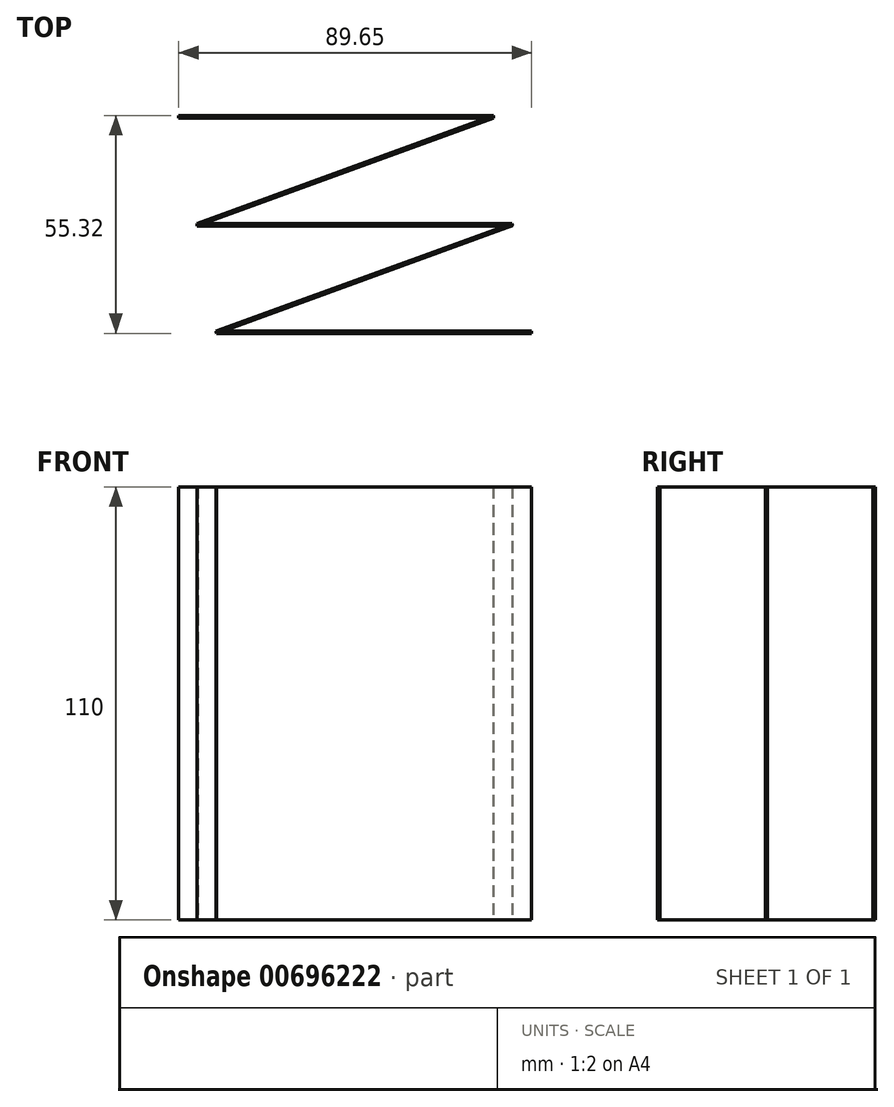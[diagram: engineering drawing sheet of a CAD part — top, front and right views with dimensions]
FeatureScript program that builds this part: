
annotation { "Feature Type Name" : "Feature", "Feature Type Description" : "" }
export const myFeature = defineFeature(function(context is Context, id is Id, definition is map)
    precondition{}
    {
        {
            var Q0;
            Q0=qCreatedBy(makeId("Front.planeOp"),FACE);
            var sketch = newSketch(context, id + "F0", { "sketchPlane" : qUnion([Q0])});
            skLineSegment(sketch, "E0.bottom", {"start": v(40, 55) * mm, "end": v(-40, 55) * mm});
            skLineSegment(sketch, "E0.top", {"start": v(40, -55) * mm, "end": v(-40, -55) * mm});
            skLineSegment(sketch, "E0.left", {"start": v(40, 55) * mm, "end": v(40, -55) * mm});
            skLineSegment(sketch, "E0.right", {"start": v(-40, 55) * mm, "end": v(-40, -55) * mm});
            skPoint(sketch, "E0.middle", {"position": v(0, 0) * mm});
            skSolve(sketch);
        }
        {
            var Q0;
            Q0=makeQuery(id+"F0.imprint","IMPRINT",FACE,{"disambiguationData":[TD([[makeQuery(id+"F0.imprint","IMPRINT",EDGE,{"derivedFrom":sQuery(id+"F0.wireOp",EDGE,"E0.bottom")}),1.0]])]});
            extrude(context, id + "F1", {"entities" : qUnion([Q0]), "depth" : 0.6 * mm, "offsetDistance" : 25 * mm});
        }
        {
            var Q0;
            Q0=makeQuery(id+"F1.opExtrude","SWEPT_BODY",BODY,{"disambiguationData":[OSD([sQuery(id+"F0.wireOp",EDGE,"E0.bottom"),sQuery(id+"F0.wireOp",EDGE,"E0.top"),sQuery(id+"F0.wireOp",EDGE,"E0.left"),sQuery(id+"F0.wireOp",EDGE,"E0.right")])]});
            var Q1;
            Q1=makeQuery(id+"F1.opExtrude","CAP_EDGE",EDGE,{"disambiguationData":[OSD([sQuery(id+"F0.wireOp",EDGE,"E0.right")])],"isStart":false});
            circularPattern(context, id + "F2", {"entities" : qUnion([Q0]), "axis" : qUnion([Q1]), "angle" : 20 * degree, "instanceCount" : 2, "oppositeDirection" : true, "equalSpace" : true});
        }
        {
            var Q0;
            Q0=makeQuery(id+"F2.opPattern","COPY",BODY,{"derivedFrom":makeQuery(id+"F1.opExtrude","SWEPT_BODY",BODY,{"disambiguationData":[OSD([sQuery(id+"F0.wireOp",EDGE,"E0.bottom"),sQuery(id+"F0.wireOp",EDGE,"E0.top"),sQuery(id+"F0.wireOp",EDGE,"E0.left"),sQuery(id+"F0.wireOp",EDGE,"E0.right")])]}),"instanceName":"1"});
            var Q1;
            Q1=makeQuery(id+"F2.opPattern","COPY",EDGE,{"derivedFrom":makeQuery(id+"F1.opExtrude","CAP_EDGE",EDGE,{"disambiguationData":[OSD([sQuery(id+"F0.wireOp",EDGE,"E0.left")])],"isStart":true}),"instanceName":"1"});
            circularPattern(context, id + "F3", {"entities" : qUnion([Q0]), "axis" : qUnion([Q1]), "angle" : 20 * degree, "instanceCount" : 2, "equalSpace" : true});
        }
        {
            var Q0;
            Q0=makeQuery(id+"F3.opPattern","COPY",BODY,{"derivedFrom":makeQuery(id+"F2.opPattern","COPY",BODY,{"derivedFrom":makeQuery(id+"F1.opExtrude","SWEPT_BODY",BODY,{"disambiguationData":[OSD([sQuery(id+"F0.wireOp",EDGE,"E0.bottom"),sQuery(id+"F0.wireOp",EDGE,"E0.top"),sQuery(id+"F0.wireOp",EDGE,"E0.left"),sQuery(id+"F0.wireOp",EDGE,"E0.right")])]}),"instanceName":"1"}),"instanceName":"1"});
            var Q1;
            Q1=makeQuery(id+"F3.opPattern","COPY",EDGE,{"derivedFrom":makeQuery(id+"F2.opPattern","COPY",EDGE,{"derivedFrom":makeQuery(id+"F1.opExtrude","CAP_EDGE",EDGE,{"disambiguationData":[OSD([sQuery(id+"F0.wireOp",EDGE,"E0.right")])],"isStart":true}),"instanceName":"1"}),"instanceName":"1"});
            circularPattern(context, id + "F4", {"entities" : qUnion([Q0]), "axis" : qUnion([Q1]), "angle" : 20 * degree, "instanceCount" : 2, "oppositeDirection" : true, "equalSpace" : true});
        }
        {
            var Q0;
            Q0=makeQuery(id+"F4.opPattern","COPY",BODY,{"derivedFrom":makeQuery(id+"F3.opPattern","COPY",BODY,{"derivedFrom":makeQuery(id+"F2.opPattern","COPY",BODY,{"derivedFrom":makeQuery(id+"F1.opExtrude","SWEPT_BODY",BODY,{"disambiguationData":[OSD([sQuery(id+"F0.wireOp",EDGE,"E0.bottom"),sQuery(id+"F0.wireOp",EDGE,"E0.top"),sQuery(id+"F0.wireOp",EDGE,"E0.left"),sQuery(id+"F0.wireOp",EDGE,"E0.right")])]}),"instanceName":"1"}),"instanceName":"1"}),"instanceName":"1"});
            var Q1;
            Q1=makeQuery(id+"F4.opPattern","COPY",EDGE,{"derivedFrom":makeQuery(id+"F3.opPattern","COPY",EDGE,{"derivedFrom":makeQuery(id+"F2.opPattern","COPY",EDGE,{"derivedFrom":makeQuery(id+"F1.opExtrude","CAP_EDGE",EDGE,{"disambiguationData":[OSD([sQuery(id+"F0.wireOp",EDGE,"E0.left")])],"isStart":false}),"instanceName":"1"}),"instanceName":"1"}),"instanceName":"1"});
            circularPattern(context, id + "F5", {"entities" : qUnion([Q0]), "axis" : qUnion([Q1]), "angle" : 20 * degree, "instanceCount" : 2, "equalSpace" : true});
        }
    });
